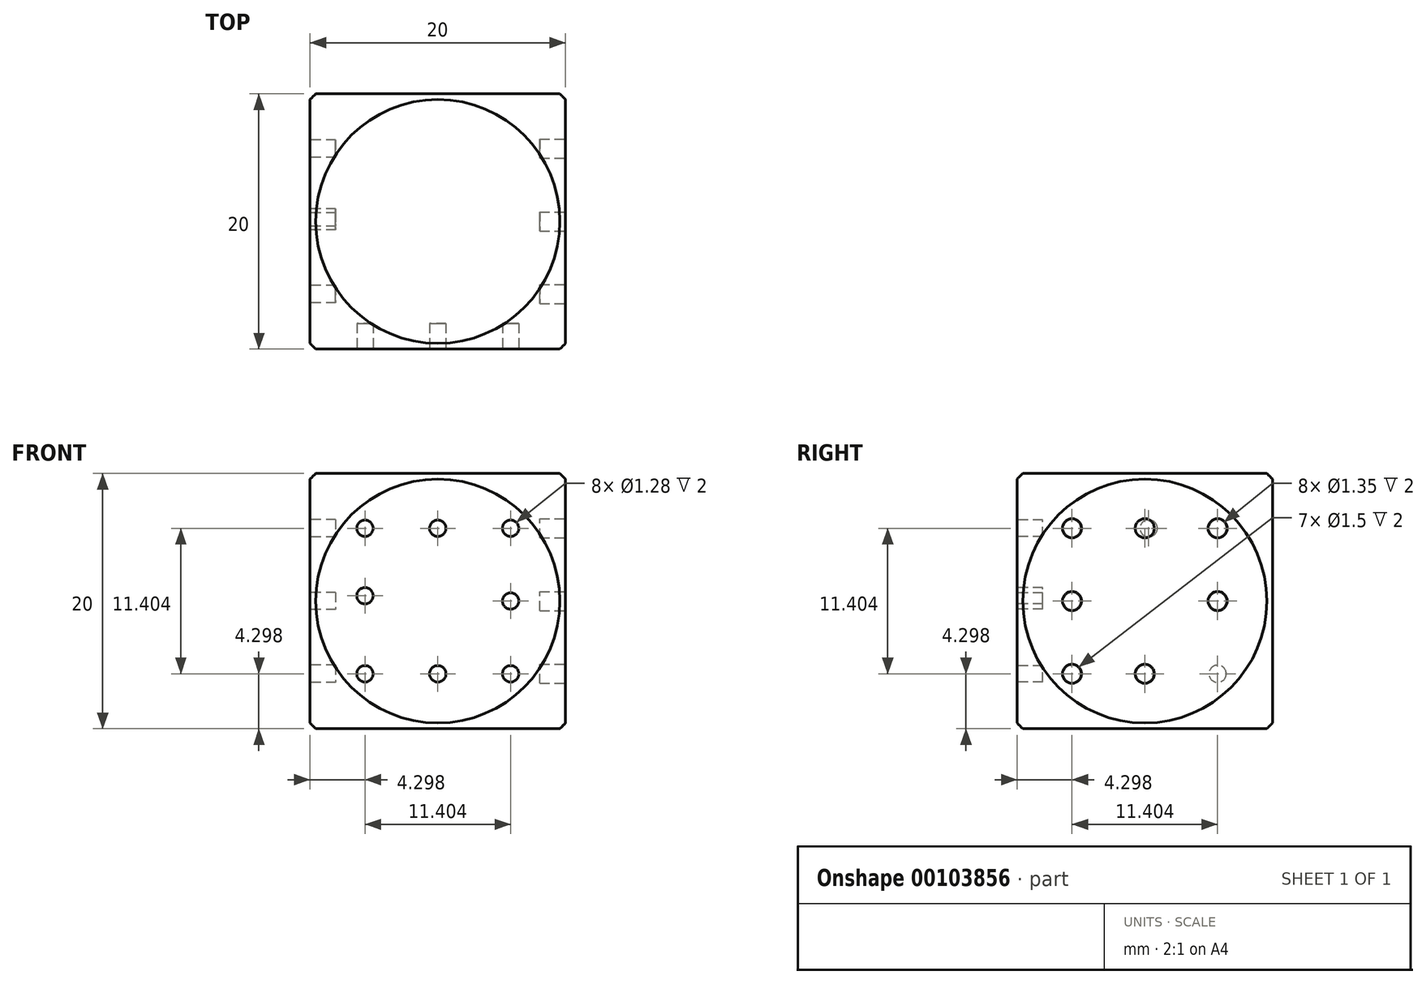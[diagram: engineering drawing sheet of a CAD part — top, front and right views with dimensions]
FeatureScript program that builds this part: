
annotation { "Feature Type Name" : "Feature", "Feature Type Description" : "" }
export const myFeature = defineFeature(function(context is Context, id is Id, definition is map)
    precondition{}
    {
        {
            var Q0;
            Q0=qCreatedBy(makeId("Front.planeOp"),FACE);
            var sketch = newSketch(context, id + "F0", { "sketchPlane" : qUnion([Q0])});
            skLineSegment(sketch, "E0.bottom", {"start": v(-10, 10) * mm, "end": v(10, 10) * mm});
            skLineSegment(sketch, "E0.top", {"start": v(-10, -10) * mm, "end": v(10, -10) * mm});
            skLineSegment(sketch, "E0.left", {"start": v(-10, 10) * mm, "end": v(-10, -10) * mm});
            skLineSegment(sketch, "E0.right", {"start": v(10, 10) * mm, "end": v(10, -10) * mm});
            skPoint(sketch, "E0.middle", {"position": v(0, 0) * mm});
            skSolve(sketch);
        }
        {
            var Q0;
            Q0 = qSketchRegion(id + "F0", true);
            extrude(context, id + "F1", {"entities" : qUnion([Q0]), "endBound" : BoundingType.SYMMETRIC, "depth" : 20 * mm});
        }
        {
            var Q0;
            Q0=qCreatedBy(makeId("Front.planeOp"),FACE);
            var sketch = newSketch(context, id + "F2", { "sketchPlane" : qUnion([Q0])});
            skArc(sketch, "E1", {"start": v(0, 13.83) * mm, "mid": v(-13.83, 0) * mm, "end": v(0, -13.83) * mm});
            skLineSegment(sketch, "E2", {"start": v(0, -21.04) * mm, "end": v(0, 23.09) * mm, "construction": true});
            skLineSegment(sketch, "E3", {"start": v(0, 13.83) * mm, "end": v(0, -13.83) * mm});
            skSolve(sketch);
        }
        {
            var Q0;
            Q0=makeQuery(id+"F2.imprint","IMPRINT",FACE,{"disambiguationData":[TD([[makeQuery(id+"F2.imprint","IMPRINT",EDGE,{"derivedFrom":sQuery(id+"F2.wireOp",EDGE,"E1")}),1.0]])]});
            var Q1;
            Q1=sQuery(id+"F2.wireOp",EDGE,"E2");
            revolve(context, id + "F3", {"operationType" : NewBodyOperationType.INTERSECT, "entities" : qUnion([Q0]), "axis" : qUnion([Q1]), "revolveType" : RevolveType.FULL});
        }
        {
            var Q0;
            Q0=makeQuery(id+"F1.opExtrude","CAP_FACE",FACE,{"disambiguationData":[OSD([sQuery(id+"F0.wireOp",EDGE,"E0.bottom"),sQuery(id+"F0.wireOp",EDGE,"E0.top"),sQuery(id+"F0.wireOp",EDGE,"E0.left"),sQuery(id+"F0.wireOp",EDGE,"E0.right")])],"isStart":true});
            var sketch = newSketch(context, id + "F4", { "sketchPlane" : qUnion([Q0])});
            skLineSegment(sketch, "E4.bottom", {"start": v(-5.7, 5.7) * mm, "end": v(5.7, 5.7) * mm});
            skLineSegment(sketch, "E4.top", {"start": v(-5.7, -5.7) * mm, "end": v(5.7, -5.7) * mm});
            skLineSegment(sketch, "E4.left", {"start": v(-5.7, 5.7) * mm, "end": v(-5.7, -5.7) * mm});
            skLineSegment(sketch, "E4.right", {"start": v(5.7, 5.7) * mm, "end": v(5.7, -5.7) * mm});
            skPoint(sketch, "E4.middle", {"position": v(0, 0) * mm});
            skSolve(sketch);
        }
        {
            var Q0;
            Q0=makeQuery(id+"F1.opExtrude","SWEPT_FACE",FACE,{"disambiguationData":[OSD([sQuery(id+"F0.wireOp",EDGE,"E0.right")])]});
            var sketch = newSketch(context, id + "F5", { "sketchPlane" : qUnion([Q0])});
            skLineSegment(sketch, "E5.bottom", {"start": v(-5.7, 5.7) * mm, "end": v(5.7, 5.7) * mm, "construction": true});
            skLineSegment(sketch, "E5.top", {"start": v(-5.7, -5.7) * mm, "end": v(5.7, -5.7) * mm, "construction": true});
            skLineSegment(sketch, "E5.left", {"start": v(-5.7, 5.7) * mm, "end": v(-5.7, -5.7) * mm, "construction": true});
            skLineSegment(sketch, "E5.right", {"start": v(5.7, 5.7) * mm, "end": v(5.7, -5.7) * mm, "construction": true});
            skPoint(sketch, "E5.middle", {"position": v(0, 0) * mm});
            skCircle(sketch, "E6", {"center": v(-5.7, 5.7) * mm, "radius": 0.75 * mm});
            skCircle(sketch, "E7", {"center": v(-5.7, 0) * mm, "radius": 0.75 * mm});
            skCircle(sketch, "E8", {"center": v(-5.7, -5.7) * mm, "radius": 0.75 * mm});
            skCircle(sketch, "E9", {"center": v(0, -5.7) * mm, "radius": 0.75 * mm});
            skCircle(sketch, "E10", {"center": v(5.7, 0) * mm, "radius": 0.75 * mm});
            skCircle(sketch, "E11", {"center": v(5.7, 5.7) * mm, "radius": 0.75 * mm});
            skCircle(sketch, "E12", {"center": v(0, 5.7) * mm, "radius": 0.75 * mm});
            skSolve(sketch);
        }
        {
            var Q0;
            Q0=makeQuery(id+"F5.imprint","IMPRINT",FACE,{"disambiguationData":[TD([[makeQuery(id+"F5.imprint","IMPRINT",EDGE,{"derivedFrom":sQuery(id+"F5.wireOp",EDGE,"E9")}),1.0]])]});
            var Q1;
            Q1=makeQuery(id+"F5.imprint","IMPRINT",FACE,{"disambiguationData":[TD([[makeQuery(id+"F5.imprint","IMPRINT",EDGE,{"derivedFrom":sQuery(id+"F5.wireOp",EDGE,"E8")}),1.0]])]});
            var Q2;
            Q2=makeQuery(id+"F5.imprint","IMPRINT",FACE,{"disambiguationData":[TD([[makeQuery(id+"F5.imprint","IMPRINT",EDGE,{"derivedFrom":sQuery(id+"F5.wireOp",EDGE,"E7")}),1.0]])]});
            var Q3;
            Q3=makeQuery(id+"F5.imprint","IMPRINT",FACE,{"disambiguationData":[TD([[makeQuery(id+"F5.imprint","IMPRINT",EDGE,{"derivedFrom":sQuery(id+"F5.wireOp",EDGE,"E6")}),1.0]])]});
            var Q4;
            Q4=makeQuery(id+"F5.imprint","IMPRINT",FACE,{"disambiguationData":[TD([[makeQuery(id+"F5.imprint","IMPRINT",EDGE,{"derivedFrom":sQuery(id+"F5.wireOp",EDGE,"E12")}),1.0]])]});
            var Q5;
            Q5=makeQuery(id+"F5.imprint","IMPRINT",FACE,{"disambiguationData":[TD([[makeQuery(id+"F5.imprint","IMPRINT",EDGE,{"derivedFrom":sQuery(id+"F5.wireOp",EDGE,"E11")}),1.0]])]});
            var Q6;
            Q6=makeQuery(id+"F5.imprint","IMPRINT",FACE,{"disambiguationData":[TD([[makeQuery(id+"F5.imprint","IMPRINT",EDGE,{"derivedFrom":sQuery(id+"F5.wireOp",EDGE,"E10")}),1.0]])]});
            extrude(context, id + "F6", {"entities" : qUnion([Q0, Q1, Q2, Q3, Q4, Q5, Q6]), "operationType" : NewBodyOperationType.REMOVE, "oppositeDirection" : true, "depth" : 2 * mm});
        }
        {
            var Q0;
            Q0=makeQuery(id+"F1.opExtrude","CAP_FACE",FACE,{"disambiguationData":[OSD([sQuery(id+"F0.wireOp",EDGE,"E0.bottom"),sQuery(id+"F0.wireOp",EDGE,"E0.top"),sQuery(id+"F0.wireOp",EDGE,"E0.left"),sQuery(id+"F0.wireOp",EDGE,"E0.right")])],"isStart":false});
            var sketch = newSketch(context, id + "F7", { "sketchPlane" : qUnion([Q0])});
            skLineSegment(sketch, "E13.bottom", {"start": v(-5.7, 5.7) * mm, "end": v(5.7, 5.7) * mm, "construction": true});
            skLineSegment(sketch, "E13.top", {"start": v(-5.7, -5.7) * mm, "end": v(5.7, -5.7) * mm, "construction": true});
            skLineSegment(sketch, "E13.left", {"start": v(-5.7, 5.7) * mm, "end": v(-5.7, -5.7) * mm, "construction": true});
            skLineSegment(sketch, "E13.right", {"start": v(5.7, 5.7) * mm, "end": v(5.7, -5.7) * mm, "construction": true});
            skPoint(sketch, "E13.middle", {"position": v(0, 0) * mm});
            skCircle(sketch, "E14", {"center": v(-5.7, 5.7) * mm, "radius": 0.64 * mm});
            skCircle(sketch, "E15", {"center": v(-5.7, 0.41) * mm, "radius": 0.64 * mm});
            skCircle(sketch, "E16", {"center": v(-5.7, -5.7) * mm, "radius": 0.64 * mm});
            skCircle(sketch, "E17", {"center": v(0, -5.7) * mm, "radius": 0.64 * mm});
            skCircle(sketch, "E18", {"center": v(5.7, -5.7) * mm, "radius": 0.64 * mm});
            skCircle(sketch, "E19", {"center": v(5.7, 0) * mm, "radius": 0.64 * mm});
            skCircle(sketch, "E20", {"center": v(5.7, 5.7) * mm, "radius": 0.64 * mm});
            skCircle(sketch, "E21", {"center": v(0, 5.7) * mm, "radius": 0.64 * mm});
            skSolve(sketch);
        }
        {
            var Q0;
            Q0=makeQuery(id+"F7.imprint","IMPRINT",FACE,{"disambiguationData":[TD([[makeQuery(id+"F7.imprint","IMPRINT",EDGE,{"derivedFrom":sQuery(id+"F7.wireOp",EDGE,"E14")}),1.0]])]});
            var Q1;
            Q1=makeQuery(id+"F7.imprint","IMPRINT",FACE,{"disambiguationData":[TD([[makeQuery(id+"F7.imprint","IMPRINT",EDGE,{"derivedFrom":sQuery(id+"F7.wireOp",EDGE,"E15")}),1.0]])]});
            var Q2;
            Q2=makeQuery(id+"F7.imprint","IMPRINT",FACE,{"disambiguationData":[TD([[makeQuery(id+"F7.imprint","IMPRINT",EDGE,{"derivedFrom":sQuery(id+"F7.wireOp",EDGE,"E16")}),1.0]])]});
            var Q3;
            Q3=makeQuery(id+"F7.imprint","IMPRINT",FACE,{"disambiguationData":[TD([[makeQuery(id+"F7.imprint","IMPRINT",EDGE,{"derivedFrom":sQuery(id+"F7.wireOp",EDGE,"E17")}),1.0]])]});
            var Q4;
            Q4=makeQuery(id+"F7.imprint","IMPRINT",FACE,{"disambiguationData":[TD([[makeQuery(id+"F7.imprint","IMPRINT",EDGE,{"derivedFrom":sQuery(id+"F7.wireOp",EDGE,"E18")}),1.0]])]});
            var Q5;
            Q5=makeQuery(id+"F7.imprint","IMPRINT",FACE,{"disambiguationData":[TD([[makeQuery(id+"F7.imprint","IMPRINT",EDGE,{"derivedFrom":sQuery(id+"F7.wireOp",EDGE,"E19")}),1.0]])]});
            var Q6;
            Q6=makeQuery(id+"F7.imprint","IMPRINT",FACE,{"disambiguationData":[TD([[makeQuery(id+"F7.imprint","IMPRINT",EDGE,{"derivedFrom":sQuery(id+"F7.wireOp",EDGE,"E20")}),1.0]])]});
            var Q7;
            Q7=makeQuery(id+"F7.imprint","IMPRINT",FACE,{"disambiguationData":[TD([[makeQuery(id+"F7.imprint","IMPRINT",EDGE,{"derivedFrom":sQuery(id+"F7.wireOp",EDGE,"E21")}),1.0]])]});
            extrude(context, id + "F8", {"entities" : qUnion([Q0, Q1, Q2, Q3, Q4, Q5, Q6, Q7]), "operationType" : NewBodyOperationType.REMOVE, "oppositeDirection" : true, "depth" : 2 * mm});
        }
        {
            var Q0;
            Q0=makeQuery(id+"F1.opExtrude","SWEPT_FACE",FACE,{"disambiguationData":[OSD([sQuery(id+"F0.wireOp",EDGE,"E0.left")])]});
            var sketch = newSketch(context, id + "F9", { "sketchPlane" : qUnion([Q0])});
            skLineSegment(sketch, "E22.bottom", {"start": v(-5.7, 5.7) * mm, "end": v(5.7, 5.7) * mm, "construction": true});
            skLineSegment(sketch, "E22.top", {"start": v(-5.7, -5.7) * mm, "end": v(5.7, -5.7) * mm, "construction": true});
            skLineSegment(sketch, "E22.left", {"start": v(-5.7, 5.7) * mm, "end": v(-5.7, -5.7) * mm, "construction": true});
            skLineSegment(sketch, "E22.right", {"start": v(5.7, 5.7) * mm, "end": v(5.7, -5.7) * mm, "construction": true});
            skPoint(sketch, "E22.middle", {"position": v(0, 0) * mm});
            skCircle(sketch, "E23", {"center": v(-0.3, 5.7) * mm, "radius": 0.68 * mm});
            skCircle(sketch, "E24", {"center": v(-5.7, 5.7) * mm, "radius": 0.68 * mm});
            skCircle(sketch, "E25", {"center": v(-5.7, 0) * mm, "radius": 0.68 * mm});
            skCircle(sketch, "E26", {"center": v(-5.7, -5.7) * mm, "radius": 0.68 * mm});
            skCircle(sketch, "E27", {"center": v(0, -5.7) * mm, "radius": 0.68 * mm});
            skCircle(sketch, "E28", {"center": v(5.7, -5.7) * mm, "radius": 0.68 * mm});
            skCircle(sketch, "E29", {"center": v(5.7, 0) * mm, "radius": 0.68 * mm});
            skCircle(sketch, "E30", {"center": v(5.7, 5.7) * mm, "radius": 0.68 * mm});
            skSolve(sketch);
        }
        {
            var Q0;
            Q0 = qSketchRegion(id + "F9", true);
            extrude(context, id + "F10", {"entities" : qUnion([Q0]), "operationType" : NewBodyOperationType.REMOVE, "oppositeDirection" : true, "depth" : 2 * mm});
        }
    });
